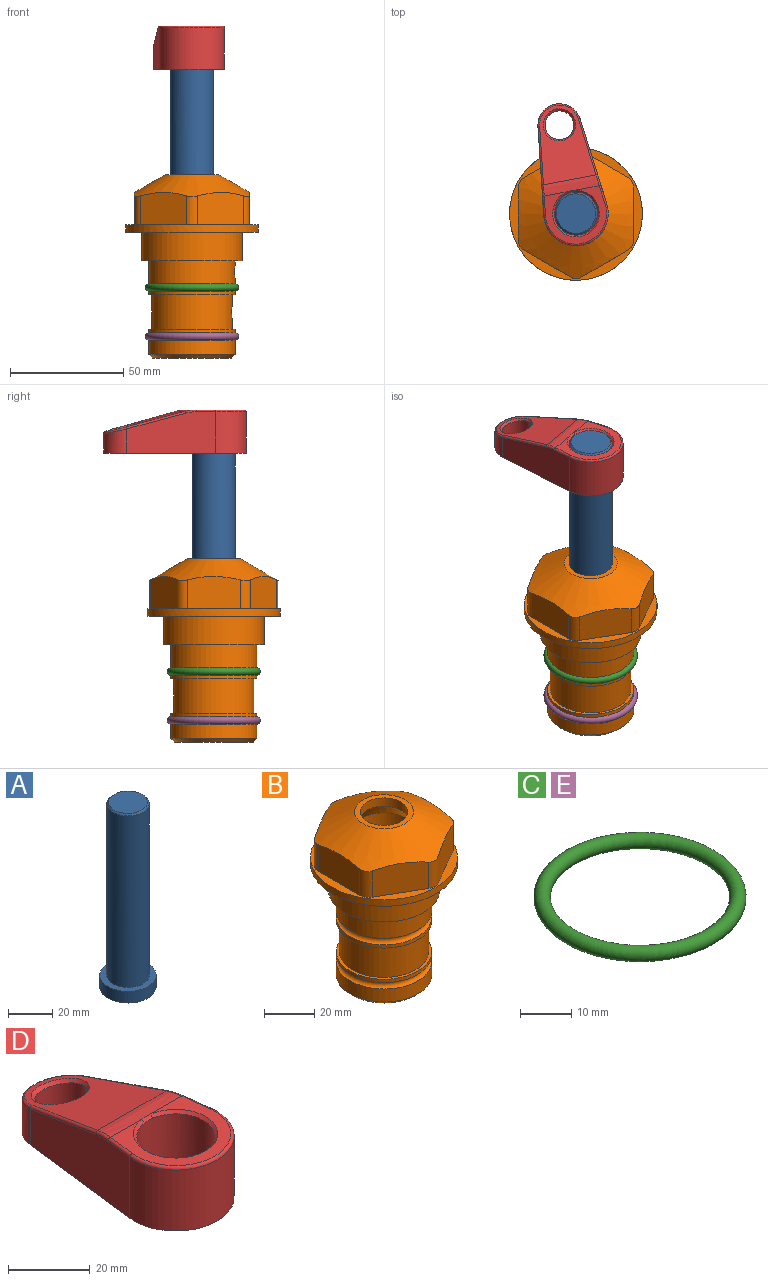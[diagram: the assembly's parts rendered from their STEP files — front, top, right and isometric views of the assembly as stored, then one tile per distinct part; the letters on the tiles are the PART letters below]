
ASSEMBLY  parts=5 mates=4
PART A: 6 faces, bbox 25.4x25.4x101.6 mm
  f0: plane 17.46x17.46mm, normal (0,0,1), area 239.5mm2, adj f5
  f1: plane 25.4x25.4mm, normal (0,0,-1), area 506.7mm2, adj f2
  f2: cylinder r=12.7mm len=25.4mm, axis (0,0,1), area 506.7mm2, adj f1,f3
  f3: plane 25.4x25.4mm, normal (0,0,1), area 221.7mm2, adj f2,f4
  f4: cylinder r=9.53mm len=94.46mm, axis (0,0,1), area 5653mm2, adj f3,f5
  f5: cone r=8.73mm half-angle=45deg, axis (0,0,-1), area 64.4mm2, adj f0,f4
PART B: 36 faces, bbox 58.7x58.7x81 mm
  f0: cylinder r=17.78mm len=35.56mm, axis (0,0,1), area 1670.8mm2, adj f23,f24,f31
  f1: cylinder r=19.05mm len=38.1mm, axis (0,0,1), area 1191.9mm2, adj f26,f27,f30
  f2: plane 58.66x58.66mm, normal (0,0,-1), area 1150.6mm2, adj f3,f28
  f3: cylinder r=29.33mm len=58.66mm, axis (0,0,-1), area 585.1mm2, adj f2,f4
  f4: plane 58.66x58.66mm, normal (0,0,1), area 475.9mm2, adj f3,f5,f6,f7,f8,f9,f10,f11
  f5: plane 20.32x14.34mm, normal (-0.5,0.87,0), area 324.4mm2, adj f4,f15,f16,f17
  f6: plane 20.32x14.34mm, normal (0.5,0.87,0), area 324.4mm2, adj f4,f14,f15,f17
  f7: plane 23.48x14.34mm, normal (1,0,0), area 324.4mm2, adj f4,f13,f14,f17
  f8: plane 20.32x14.34mm, normal (0.5,-0.87,0), area 324.4mm2, adj f4,f12,f13,f17
  f9: plane 20.32x14.34mm, normal (-0.5,-0.87,0), area 324.4mm2, adj f4,f11,f12,f17
  f10: plane 23.48x14.34mm, normal (-1,0,0), area 324.4mm2, adj f4,f11,f16,f17
  f11: cylinder r=5.08mm len=12.85mm, axis (0,0,-1), area 67.2mm2, adj f4,f9,f10,f17
  f12: cylinder r=5.08mm len=12.85mm, axis (0,0,-1), area 67.2mm2, adj f4,f8,f9,f17
  f13: cylinder r=5.08mm len=12.85mm, axis (0,0,-1), area 67.2mm2, adj f4,f7,f8,f17
  f14: cylinder r=5.08mm len=12.85mm, axis (0,0,-1), area 67.2mm2, adj f4,f6,f7,f17
  f15: cylinder r=5.08mm len=12.85mm, axis (0,0,-1), area 67.2mm2, adj f4,f5,f6,f17
  f16: cylinder r=5.08mm len=12.85mm, axis (0,0,-1), area 67.2mm2, adj f4,f5,f10,f17
  f17: cone r=11.73mm half-angle=60deg, axis (0,0,-1), area 2071.8mm2, adj f5,f6,f7,f8,f9,f10,f11,f12
  f18: plane 23.46x23.46mm, normal (0,0,1), area 147.4mm2, adj f17,f35
  f19: plane 34.93x34.93mm, normal (0,0,-1), area 958mm2, adj f29
  f20: cylinder r=19.05mm len=38.1mm, axis (0,0,1), area 760.1mm2, adj f21,f29
  f21: torus R=19.05mm, axis (0,0,1), area 565.3mm2, adj f20,f22
  f22: cylinder r=19.05mm len=38.1mm, axis (0,0,1), area 190mm2, adj f21,f23
  f23: plane 38.1x38.1mm, normal (0,0,1), area 146.9mm2, adj f0,f22
  f24: plane 38.1x38.1mm, normal (0,0,-1), area 146.9mm2, adj f0,f25
  f25: cylinder r=19.05mm len=38.1mm, axis (0,0,1), area 190mm2, adj f24,f26
  f26: torus R=19.05mm, axis (0,0,1), area 565.3mm2, adj f1,f25
  f27: plane 44.45x44.45mm, normal (0,0,-1), area 411.7mm2, adj f1,f28
  f28: cylinder r=22.23mm len=44.45mm, axis (0,0,1), area 1773.5mm2, adj f2,f27
  f29: cone r=19.05mm half-angle=45deg, axis (0,0,1), area 257.5mm2, adj f19,f20
  f30: cylinder r=3.17mm len=6.75mm, axis (-1,0,0), area 128mm2, adj f1,f33
  f31: cylinder r=3.17mm len=6.35mm, axis (-1,0,0), area 102.5mm2, adj f0,f33
  f32: plane 25.4x25.4mm, normal (0,0,1), area 506.7mm2, adj f33
  f33: cylinder r=12.7mm len=66.42mm, axis (0,0,-1), area 5236.2mm2, adj f30,f31,f32,f34
  f34: cone r=9.53mm half-angle=30deg, axis (0,0,-1), area 443.4mm2, adj f33,f35
  f35: cylinder r=9.53mm len=19.05mm, axis (0,0,-1), area 240.9mm2, adj f18,f34
PART C: 1 faces, bbox 44.7x44.7x3.2 mm
  f0: torus R=19.05mm, axis (0,0,1), area 1193.9mm2
PART D: 31 faces, bbox 31.7x65.5x19.8 mm
  f0: plane 39.12x18.26mm, normal (0.99,0.12,0), area 612.2mm2, adj f1,f4,f7,f11,f13,f15
  f1: cylinder r=9.53mm len=18.91mm, axis (0,0,-1), area 296.1mm2, adj f0,f2,f7,f17
  f2: plane 39.12x18.26mm, normal (-0.99,0.12,0), area 612.2mm2, adj f1,f4,f7,f12,f14,f16
  f3: cylinder r=6.35mm len=12.7mm, axis (0,0,-1), area 362.4mm2, adj f7,f18
  f4: cylinder r=14.29mm len=28.58mm, axis (0,0,-1), area 882.2mm2, adj f0,f2,f7,f10
  f5: cylinder r=9.53mm len=19.05mm, axis (0,0,-1), area 1092.6mm2, adj f7,f19,f20
  f6: plane 26.99x23.69mm, normal (0,0,1), area 216.2mm2, adj f9,f10,f11,f12,f19
  f7: plane 63.5x28.58mm, normal (0,0,-1), area 661.8mm2, adj f0,f1,f2,f3,f4,f5,f22,f23
  f8: plane 33.52x23.6mm, normal (0,0.26,0.97), area 486mm2, adj f9,f15,f16,f17,f18
  f9: cylinder r=19.05mm len=24.72mm, axis (1,0,0), area 120.4mm2, adj f6,f8,f13,f14,f20
  f10: torus R=13.49mm, axis (0,0,1), area 59mm2, adj f4,f6,f11,f12
  f11: cylinder r=0.79mm len=8.67mm, axis (0.12,-0.99,0), area 10.8mm2, adj f0,f6,f10,f13
  f12: cylinder r=0.79mm len=8.67mm, axis (0.12,0.99,0), area 10.8mm2, adj f2,f6,f10,f14
  f13: bspline ~4.95x1.42mm, area 6.1mm2, adj f0,f9,f11,f15
  f14: bspline ~4.95x1.42mm, area 6.1mm2, adj f2,f9,f12,f16
  f15: cylinder r=0.79mm len=25.95mm, axis (0.12,-0.96,0.26), area 32.9mm2, adj f0,f8,f13,f17
  f16: cylinder r=0.79mm len=25.95mm, axis (0.12,0.96,-0.26), area 32.9mm2, adj f2,f8,f14,f17
  f17: bspline ~18.91x8.38mm, area 30mm2, adj f1,f8,f15,f16
  f18: bspline ~14.29x14.29mm, area 48.3mm2, adj f3,f8
  f19: cone r=9.53mm half-angle=45deg, axis (0,0,1), area 66.5mm2, adj f5,f6,f20
  f20: bspline ~3.22x0.96mm, area 3.5mm2, adj f5,f9,f19
  f21: plane 2.75x2.72mm, normal (0,0,-1), area 2.9mm2, adj f23,f25,f28
  f22: plane 23.05x15.88mm, normal (-0.99,-0.12,0), area 323.6mm2, adj f7,f25,f26,f27,f28,f29
  f23: plane 23.05x15.88mm, normal (0.99,-0.12,0), area 323.6mm2, adj f7,f21,f25,f27,f28,f30
  f24: cylinder r=9.53mm len=10.69mm, axis (0,0,-1), area 114.7mm2, adj f7,f27,f29,f30
  f25: cylinder r=12.7mm len=20.59mm, axis (0,0,-1), area 381.1mm2, adj f7,f21,f22,f23,f26,f28
  f26: plane 2.75x2.72mm, normal (0,0,-1), area 2.9mm2, adj f22,f25,f28
  f27: plane 19.72x18.37mm, normal (0,-0.26,-0.97), area 291.8mm2, adj f22,f23,f24,f28,f29,f30
  f28: cylinder r=15.88mm len=19.92mm, axis (1,0,0), area 54.8mm2, adj f21,f22,f23,f25,f26,f27
  f29: cylinder r=1.59mm len=11mm, axis (0,0,-1), area 34.7mm2, adj f7,f22,f24,f27
  f30: cylinder r=1.59mm len=11mm, axis (0,0,-1), area 34.7mm2, adj f7,f23,f24,f27
PART E: same geometry as C
PLACE A rot(axis=(0,0,1),10.6deg) t=(0,0,27.55)mm
PLACE B at identity fixed
PLACE C at identity
PLACE D rot(axis=(0,0,1),10.6deg) t=(0,0,27.55)mm
PLACE E t=(0,0,-21.59)mm
MATE fastened A.f2 <-> D.f4  axis (0,0,1) through (0,0,91.05)mm
MATE fastened C.f0 <-> B.f0  axis (0,0,1) through (0,0,-24.51)mm
MATE fastened E.f0 <-> B.f0  axis (0,0,1) through (0,0,-46.1)mm
MATE cylindrical B.f0 <-> A.f2  axis (0,0,1) through (0,0,-50.55)mm
